# Revit family: Midea_VRF_Indoor_4-way Cassette_MI-28(36,45)Q4_DHN1-D (2nd DC)-360°
name_source: partatom
category: Equipamento mecânico
units: mm (PartAtom-declared; Revit-internal decimal feet)

## family parameters
Com base no plano de trabalho = Não
Compartilhado = Não
Corte com vazios quando carregada = Não
Cota do conector redondo = Utilizar diâmetro
Número OmniClass = 23.75.00.00
Ponto de cálculo do ambiente = Não
Sempre na vertical = Sim
Tipo de parte = Normal
Título OmniClass = Climate Control (HVAC)

## types (3) — shared parameters
Condensation = air
Depth = 840  [stored 2.75591 ft]
Descrição = High efficiency air cooled
Drain pipe = 32  [stored 0.104987 ft]
Fabricante = Trane
Gas = R410a
Gas pipe = 12.7  [stored 0.0416667 ft]
Height = 230  [stored 0.754593 ft]
Installation = Indoor installation
Liquid pipe = 6.35  [stored 0.0208333 ft]
Machine material = grilles：ABS/HIPS
Maximum Fuse Amps = 15 A
Panel color = S1004
Power supply = 220-240V ~50/60Hz
Series = Ultra
URL = https://www.trane.com
Width = 840  [stored 2.75591 ft]
clearance access behind = 1000  [stored 3.28084 ft]
clearance access front = 1000  [stored 3.28084 ft]
clearance access left = 1000  [stored 3.28084 ft]
clearance access right = 1000  [stored 3.28084 ft]

## per-type parameters (varying)
| type | Air Flow | Cooling Capacity | Cooling Power Input | Gross Weight | Heating Capacity | Heating Power Input | Minimum Circuit Amps |
| 4TVC0009EF000AA | 982/935/877/832/788/732/677 m3/h | 2.80 kW | 25 W | 21.30 kg | 3.20 kW | 25 W | 0 A |
| 4TVC0012EF000AA | 982/935/877/832/788/732/677 m3/h | 3.60 kW | 25 W | 21.30 kg | 4.00 kW | 25 W | 0 A |
| 4TVC0015EF000AA | 1029/957/899/857/801/756/704 m3/h | 4.50 kW | 31 W | 23.20 kg | 5.00 kW | 31 W | 1 A |

note: column(s) folded — value = type name in every type: Modelo

note: [stored X ft] marks values corroborated as IEEE doubles in the binary element streams (Revit-internal decimal feet)

## geometry (parser evidence)
native form markers: Blend x2, Sweep x11
no freeform markers — native parametric forms only
